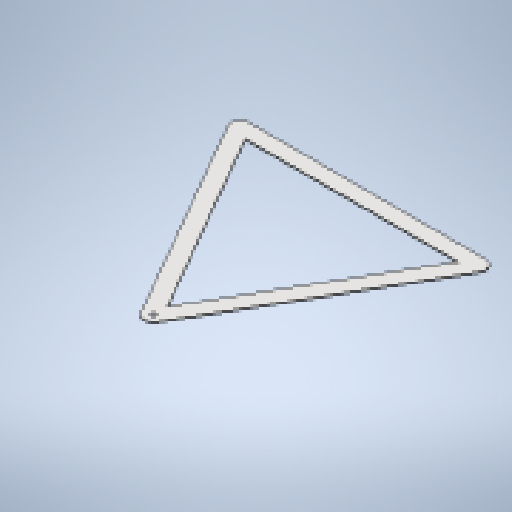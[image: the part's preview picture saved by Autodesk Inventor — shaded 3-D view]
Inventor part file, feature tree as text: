
AUTODESK INVENTOR PART (.ipt)
format: ipt  version: 2025.1 (Build 291241020, 241B)  size: 197,120 bytes
history: native  units: mm
features: other x2, sheet_metal_op x1, chamfer x1, sketch x1
ambient origin geometry x8: Origin, YZ Plane, XZ Plane, XY Plane, X Axis, Y Axis, Z Axis, Center Point
bodies: Solid1 (feature_tree)
feature tree (5):
  sheet_metal_op  "Face1"
  chamfer  "Corner Round3"
  sketch  "Sketch1"  dims[d2=3.0mm d34=17.0mm d35=20.0mm d36=1000.25mm d37=1000.25mm d38=50.0mm d39=17.0mm d40=17.0mm d41=6.0mm]
  other  "Plate1"
  other  "Definition1"
